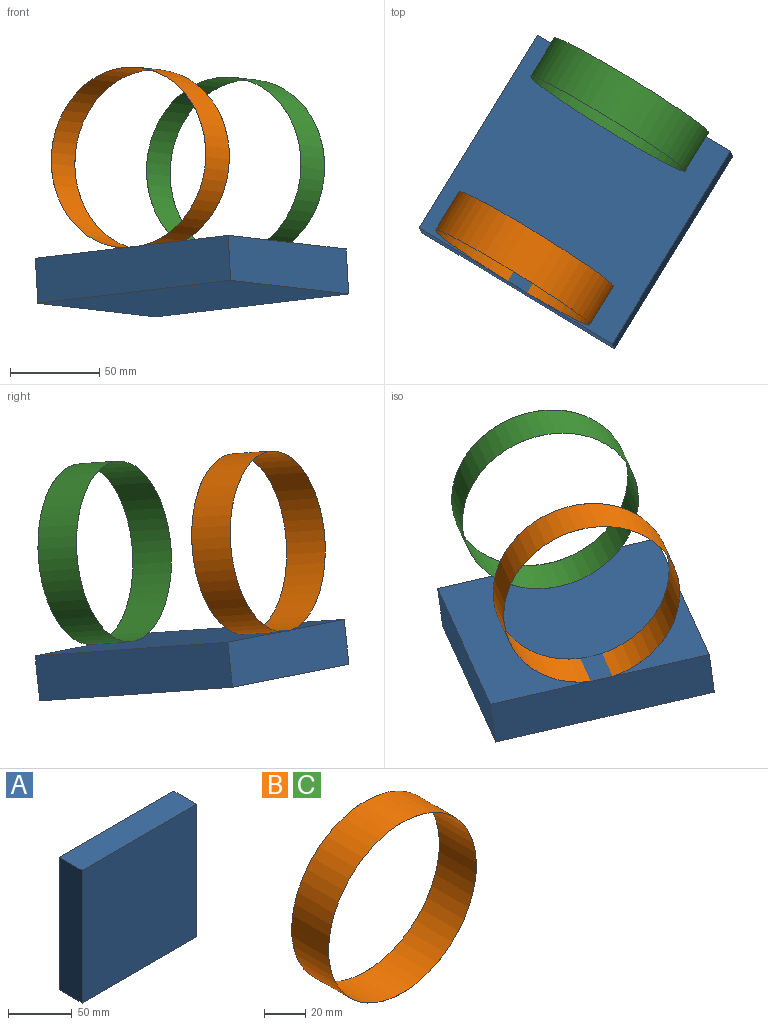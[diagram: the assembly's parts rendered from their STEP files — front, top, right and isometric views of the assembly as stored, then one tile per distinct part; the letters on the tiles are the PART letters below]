
ASSEMBLY  parts=3 mates=3
PART A: 6 faces, bbox 127x25.4x127 mm
  f0: plane 127x25.4mm, normal (1,0,0), area 3225.8mm2, adj f1,f3,f4,f5
  f1: plane 127x25.4mm, normal (0,0,1), area 3225.8mm2, adj f0,f2,f4,f5
  f2: plane 127x25.4mm, normal (-1,0,0), area 3225.8mm2, adj f1,f3,f4,f5
  f3: plane 127x25.4mm, normal (0,0,-1), area 3225.8mm2, adj f0,f2,f4,f5
  f4: plane 127x127mm, normal (0,-1,0), area 16129mm2, adj f0,f1,f2,f3
  f5: plane 127x127mm, normal (0,1,0), area 16129mm2, adj f0,f1,f2,f3
PART B: 4 faces, bbox 101.6x25.4x101.6 mm
  f0: cylinder r=50.77mm len=101.55mm, axis (0,1,0), area 8103.3mm2, adj f2,f3
  f1: cylinder r=50.8mm len=101.6mm, axis (0,1,0), area 8107.3mm2, adj f2,f3
  f2: plane 101.6x101.6mm, normal (0,-1,0), area 8.1mm2, adj f0,f1
  f3: plane 101.6x101.6mm, normal (0,1,0), area 8.1mm2, adj f0,f1
PART C: same geometry as B
PLACE A rot(axis=(-0.22,-0.66,0.72),161.4deg) t=(-123.75,-67.68,-127.37)mm
PLACE B rot(axis=(0.92,-0.25,0.3),166.9deg) t=(-160.07,-114.45,-48.2)mm
PLACE C rot(axis=(0.92,-0.25,0.3),166.9deg) t=(-106.64,-28.21,-53.81)mm
MATE planar A.f1 <-> B.f1  axis (-0.52,-0.85,0.06) through (-157.54,-120.42,-110.94)mm
MATE parallel B.f0 <-> C.f0  axis (0.52,0.85,-0.06) through (-146.83,-92.83,-49.73)mm
MATE planar A.f3 <-> C.f0  axis (0.52,0.85,-0.06) through (-91.36,-12.3,-118.57)mm
